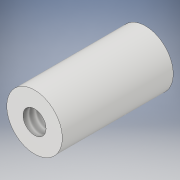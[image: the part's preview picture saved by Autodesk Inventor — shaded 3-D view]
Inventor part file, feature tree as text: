
AUTODESK INVENTOR PART (.ipt)
format: ipt  version: 2019.4 (Build 234330000, 330)  size: 100,352 bytes
history: native  units: in
note: dims shown in document units (in); Inventor stores cm internally (conversion verified against a paired STEP export)
features: sketch x2, extrude x1, hole x1
ambient origin geometry x8: Origin, YZ Plane, XZ Plane, XY Plane, X Axis, Y Axis, Z Axis, Center Point
bodies: Solid1 (feature_tree)
feature tree (4):
  extrude  "Extrusion1"  Depth=0.5in TaperAngle=0.0deg
  hole  "Hole1"  [1 undecoded]
  sketch  "Sketch1"  dims[d0=0.25in d1=0.5in d2=0.0in]
  sketch  "Sketch2"  dims[d3=0.104in d4=0.276in d5=0.375in d6=0.25in d7=0.5635in d8=0.432in d9=0.8108in]
note: 1 required parameter value undecoded (feature->parameter linkage not recoverable at this tier; creation-order binding heuristic only, values carry confidence <= 0.55)
